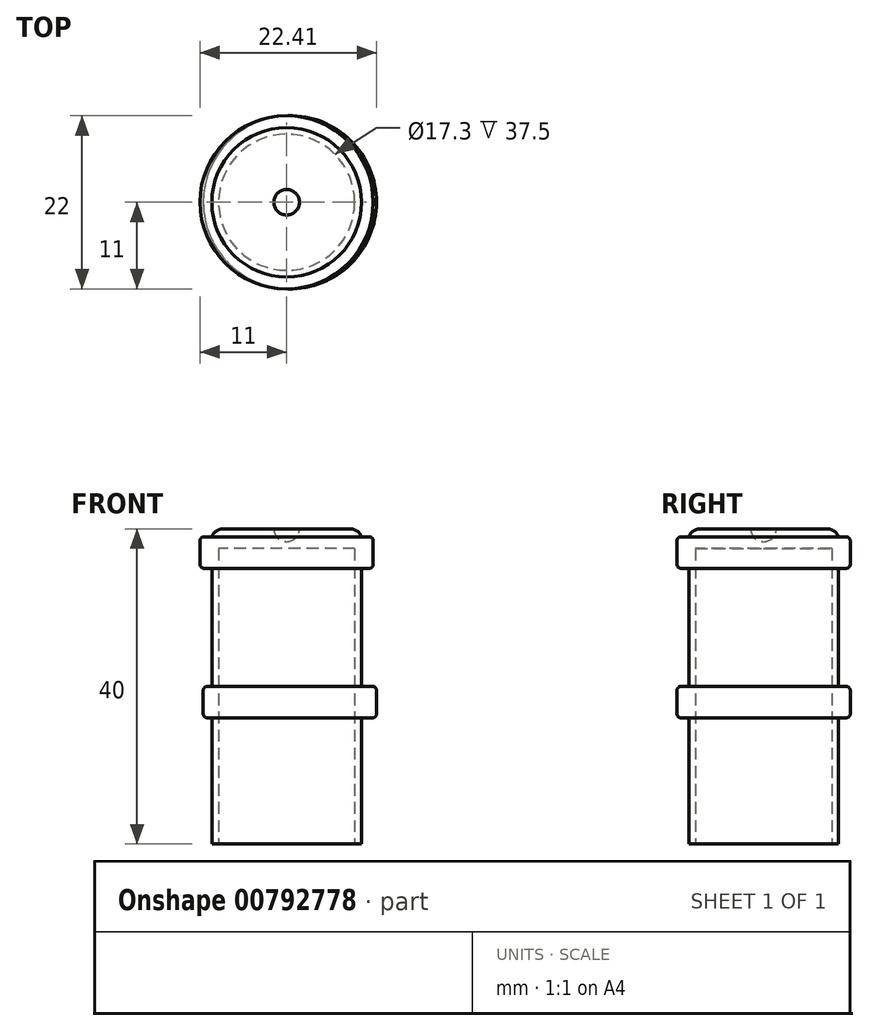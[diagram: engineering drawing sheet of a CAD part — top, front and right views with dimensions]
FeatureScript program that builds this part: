
annotation { "Feature Type Name" : "Feature", "Feature Type Description" : "" }
export const myFeature = defineFeature(function(context is Context, id is Id, definition is map)
    precondition{}
    {
        {
            var Q0;
            Q0=qCreatedBy(makeId("Top.planeOp"),FACE);
            var sketch = newSketch(context, id + "F0", { "sketchPlane" : qUnion([Q0])});
            skCircle(sketch, "E0", {"center": v(0, 0) * mm, "radius": 9.5 * mm});
            skSolve(sketch);
        }
        {
            var Q0;
            Q0=makeQuery(id+"F0.imprint","IMPRINT",FACE,{"disambiguationData":[TD([[makeQuery(id+"F0.imprint","IMPRINT",EDGE,{"derivedFrom":sQuery(id+"F0.wireOp",EDGE,"E0")}),1.0]])]});
            var sketch = newSketch(context, id + "F1", { "sketchPlane" : qUnion([Q0])});
            skCircle(sketch, "E1", {"center": v(0, 0) * mm, "radius": 8.65 * mm});
            skSolve(sketch);
        }
        {
            var Q0;
            Q0 = qSketchRegion(id + "F0", true);
            extrude(context, id + "F2", {"entities" : qUnion([Q0]), "depth" : (40 - 24) * mm, "offsetDistance" : 25 * mm});
        }
        {
            var Q0;
            Q0=makeQuery(id+"F2.opExtrude","CAP_FACE",FACE,{"disambiguationData":[OSD([sQuery(id+"F0.wireOp",EDGE,"E0")])],"isStart":false});
            var sketch = newSketch(context, id + "F3", { "sketchPlane" : qUnion([Q0])});
            skCircle(sketch, "E2", {"center": v(0.41, 0) * mm, "radius": 11 * mm});
            skSolve(sketch);
        }
        {
            var Q0;
            Q0 = qSketchRegion(id + "F3", true);
            extrude(context, id + "F4", {"entities" : qUnion([Q0]), "operationType" : NewBodyOperationType.ADD, "depth" : 4 * mm, "offsetDistance" : 25 * mm});
        }
        {
            var Q0;
            Q0=makeQuery(id+"F4.opExtrude","CAP_FACE",FACE,{"disambiguationData":[OSD([sQuery(id+"F3.wireOp",EDGE,"E2")])],"isStart":false});
            var sketch = newSketch(context, id + "F5", { "sketchPlane" : qUnion([Q0])});
            skCircle(sketch, "E3", {"center": v(0, 0) * mm, "radius": 9.5 * mm});
            skSolve(sketch);
        }
        {
            var Q0;
            Q0 = qSketchRegion(id + "F5", true);
            extrude(context, id + "F6", {"entities" : qUnion([Q0]), "operationType" : NewBodyOperationType.ADD, "depth" : 15 * mm, "offsetDistance" : 25 * mm});
        }
        {
            var Q0;
            Q0=makeQuery(id+"F6.opExtrude","CAP_FACE",FACE,{"disambiguationData":[OSD([sQuery(id+"F5.wireOp",EDGE,"E3")])],"isStart":false});
            var sketch = newSketch(context, id + "F7", { "sketchPlane" : qUnion([Q0])});
            skCircle(sketch, "E4", {"center": v(0, 0) * mm, "radius": 11 * mm});
            skSolve(sketch);
        }
        {
            var Q0;
            Q0 = qSketchRegion(id + "F7", true);
            extrude(context, id + "F8", {"entities" : qUnion([Q0]), "operationType" : NewBodyOperationType.ADD, "depth" : 4 * mm, "offsetDistance" : 25 * mm});
        }
        {
            var Q0;
            Q0=makeQuery(id+"F8.opExtrude","CAP_FACE",FACE,{"disambiguationData":[OSD([sQuery(id+"F7.wireOp",EDGE,"E4")])],"isStart":false});
            var sketch = newSketch(context, id + "F9", { "sketchPlane" : qUnion([Q0])});
            skCircle(sketch, "E5", {"center": v(0, 0) * mm, "radius": 9.5 * mm});
            skSolve(sketch);
        }
        {
            var Q0;
            Q0 = qSketchRegion(id + "F9", true);
            extrude(context, id + "F10", {"entities" : qUnion([Q0]), "operationType" : NewBodyOperationType.ADD, "depth" : 1 * mm, "offsetDistance" : 25 * mm});
        }
        {
            var Q0;
            Q0=makeQuery(id+"F2.opExtrude","CAP_EDGE",EDGE,{"disambiguationData":[OSD([sQuery(id+"F0.wireOp",EDGE,"E0")])],"isStart":false});
            var Q1;
            Q1=makeQuery(id+"F4.opExtrude","CAP_EDGE",EDGE,{"disambiguationData":[OSD([sQuery(id+"F3.wireOp",EDGE,"E2")])],"isStart":true});
            var Q2;
            Q2=makeQuery(id+"F4.opExtrude","CAP_EDGE",EDGE,{"disambiguationData":[OSD([sQuery(id+"F3.wireOp",EDGE,"E2")])],"isStart":false});
            var Q3;
            Q3=makeQuery(id+"F6.opExtrude","CAP_EDGE",EDGE,{"disambiguationData":[OSD([sQuery(id+"F5.wireOp",EDGE,"E3")])],"isStart":true});
            var Q4;
            Q4=makeQuery(id+"F6.opExtrude","CAP_EDGE",EDGE,{"disambiguationData":[OSD([sQuery(id+"F5.wireOp",EDGE,"E3")])],"isStart":false});
            var Q5;
            Q5=makeQuery(id+"F8.opExtrude","CAP_EDGE",EDGE,{"disambiguationData":[OSD([sQuery(id+"F7.wireOp",EDGE,"E4")])],"isStart":true});
            var Q6;
            Q6=makeQuery(id+"F8.opExtrude","CAP_EDGE",EDGE,{"disambiguationData":[OSD([sQuery(id+"F7.wireOp",EDGE,"E4")])],"isStart":false});
            var Q7;
            Q7=makeQuery(id+"F10.opExtrude","CAP_EDGE",EDGE,{"disambiguationData":[OSD([sQuery(id+"F9.wireOp",EDGE,"E5")])],"isStart":true});
            fillet(context, id + "F11", {"entities" : qUnion([Q0, Q1, Q2, Q3, Q4, Q5, Q6, Q7]), "radius" : 0.5 * mm, "tangentPropagation" : true, "allowEdgeOverflow" : false});
        }
        {
            var Q0;
            Q0=makeQuery(id+"F10.opExtrude","CAP_EDGE",EDGE,{"disambiguationData":[OSD([sQuery(id+"F9.wireOp",EDGE,"E5")])],"isStart":false});
            fillet(context, id + "F12", {"entities" : qUnion([Q0]), "radius" : 1.5 * mm, "tangentPropagation" : true, "allowEdgeOverflow" : false});
        }
        {
            var Q0;
            Q0 = qSketchRegion(id + "F1", true);
            extrude(context, id + "F13", {"entities" : qUnion([Q0]), "operationType" : NewBodyOperationType.REMOVE, "depth" : 37.5 * mm, "offsetDistance" : 25 * mm});
        }
        {
            var Q0;
            Q0=qCreatedBy(makeId("Front.planeOp"),FACE);
            var sketch = newSketch(context, id + "F14", { "sketchPlane" : qUnion([Q0])});
            skArc(sketch, "E6", {"start": v(1.62, 40) * mm, "mid": v(0, 41.63) * mm, "end": v(-1.63, 40) * mm});
            skLineSegment(sketch, "E7", {"start": v(-2.83, 40) * mm, "end": v(2.95, 40) * mm});
            skSolve(sketch);
        }
        {
            var Q0;
            {var subQ0=sQuery(id+"F14.wireOp",EDGE,"E6");Q0=makeQuery(id+"F14.imprint","IMPRINT",FACE,{"disambiguationData":[TD([[makeQuery(id+"F14.imprint","IMPRINT",EDGE,{"derivedFrom":subQ0}),1.0]])]});}
            var Q1;
            Q1=sQuery(id+"F14.wireOp",EDGE,"E7");
            revolve(context, id + "F15", {"operationType" : NewBodyOperationType.REMOVE, "surfaceOperationType" : NewSurfaceOperationType.NEW, "entities" : qUnion([Q0]), "axis" : qUnion([Q1]), "revolveType" : RevolveType.FULL, "oppositeDirection" : true});
        }
    });
